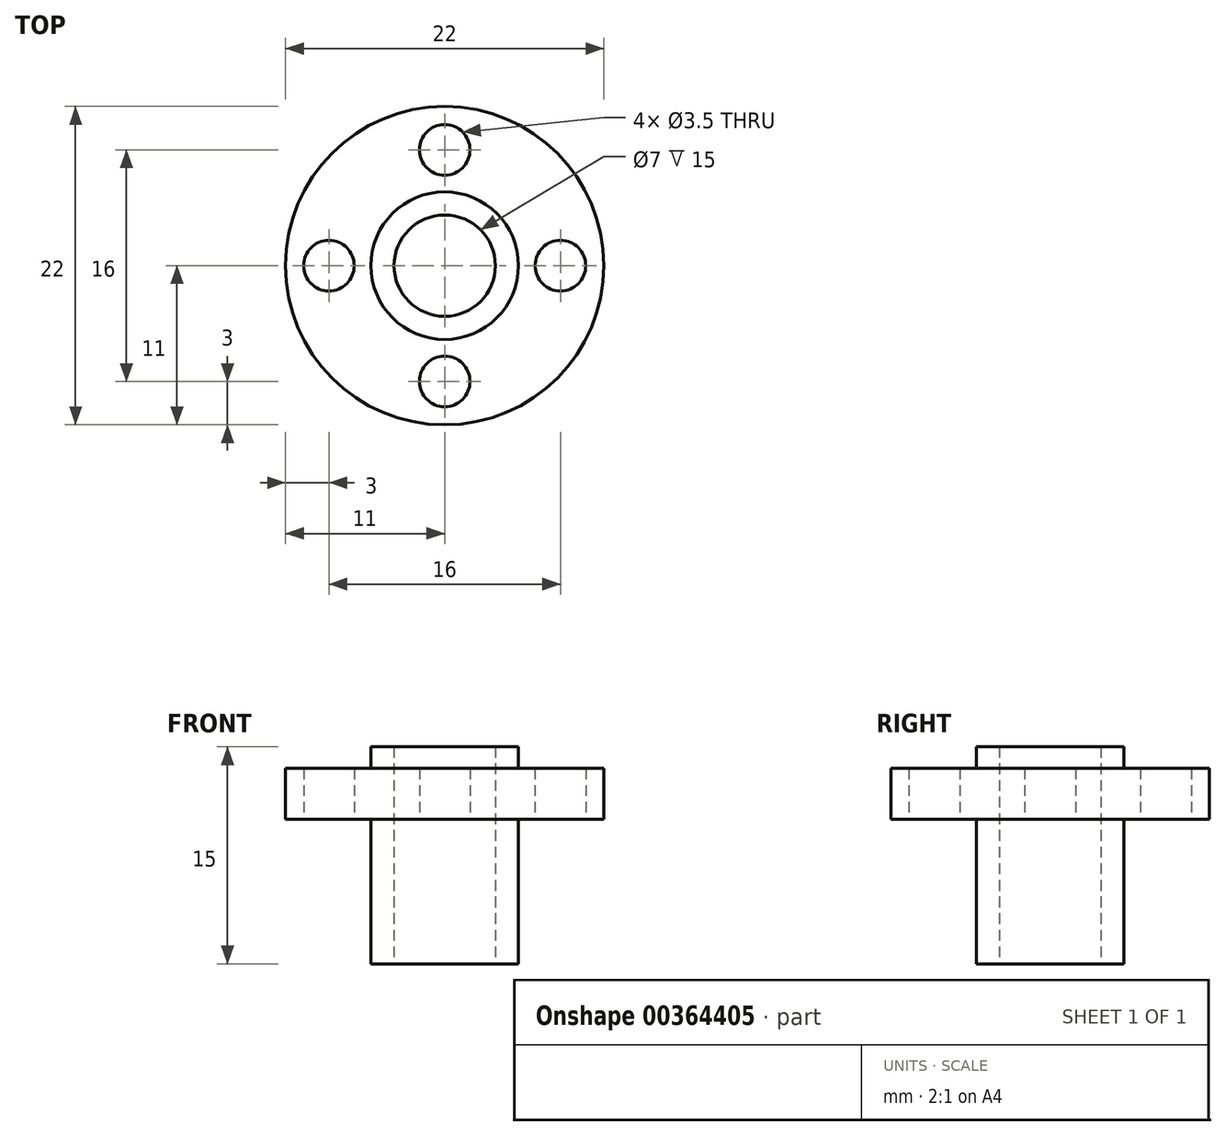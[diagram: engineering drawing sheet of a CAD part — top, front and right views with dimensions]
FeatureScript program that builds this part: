
annotation { "Feature Type Name" : "Feature", "Feature Type Description" : "" }
export const myFeature = defineFeature(function(context is Context, id is Id, definition is map)
    precondition{}
    {
        {
            var Q0;
            Q0=qCreatedBy(makeId("Top.planeOp"),FACE);
            var sketch = newSketch(context, id + "F0", { "sketchPlane" : qUnion([Q0])});
            skCircle(sketch, "E0", {"center": v(0, 0) * mm, "radius": 11 * mm});
            skCircle(sketch, "E1", {"center": v(0, 0) * mm, "radius": 8 * mm, "construction": true});
            skCircle(sketch, "E2", {"center": v(0, 0) * mm, "radius": 5.1 * mm});
            skCircle(sketch, "E3", {"center": v(0, 8) * mm, "radius": 1.75 * mm});
            skCircle(sketch, "E4.1.0", {"center": v(-8, 0) * mm, "radius": 1.75 * mm});
            skCircle(sketch, "E4.2.0", {"center": v(0, -8) * mm, "radius": 1.75 * mm});
            skCircle(sketch, "E4.3.0", {"center": v(8, 0) * mm, "radius": 1.75 * mm});
            skCircle(sketch, "E5", {"center": v(0, 0) * mm, "radius": 3.5 * mm});
            skSolve(sketch);
        }
        {
            var Q0;
            Q0=qSketchRegion(id+"F0",true);
            extrude(context, id + "F1", {"entities" : qUnion([Q0]), "depth" : 3.5 * mm});
        }
        {
            var Q0;
            Q0=makeQuery(id+"F0.imprint","IMPRINT",FACE,{"disambiguationData":[TD([[makeQuery(id+"F0.imprint","IMPRINT",EDGE,{"derivedFrom":sQuery(id+"F0.wireOp",EDGE,"E2")}),1.0]])]});
            extrude(context, id + "F2", {"entities" : qUnion([Q0]), "operationType" : NewBodyOperationType.ADD, "depth" : (3.5 + 1.5) * mm});
        }
        {
            var Q0;
            Q0=makeQuery(id+"F0.imprint","IMPRINT",FACE,{"disambiguationData":[TD([[makeQuery(id+"F0.imprint","IMPRINT",EDGE,{"derivedFrom":sQuery(id+"F0.wireOp",EDGE,"E2")}),1.0]])]});
            extrude(context, id + "F3", {"entities" : qUnion([Q0]), "operationType" : NewBodyOperationType.ADD, "oppositeDirection" : true, "depth" : 10 * mm});
        }
    });
